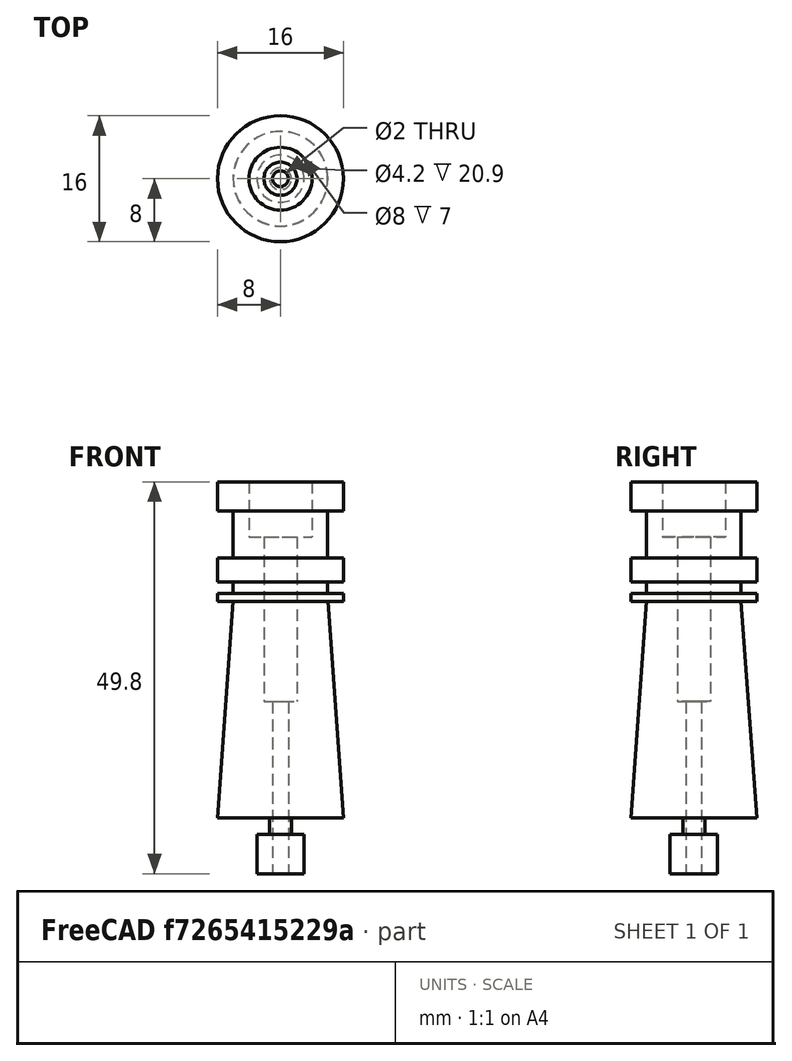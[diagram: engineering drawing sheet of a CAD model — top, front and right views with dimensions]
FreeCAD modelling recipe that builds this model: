
FCSTD DOCUMENT  (FreeCAD 0.15R4671 (Git))
Label: e3d_cuerpo
License: CreativeCommons Attribution-ShareAlike
LicenseURL: http://creativecommons.org/licenses/by-sa/4.0/
objects: Sketcher::SketchObject×1, PartDesign::Revolution×1, Part::Feature×1
note: 4 computed .brp shape members not serialized (recipe doc carries the construction recipe); baked Part::Feature solids carry a one-line shape summary decoded from their .brp

FEATURE [Sketcher::SketchObject] Sketch
  Placement = pos=(0,0,0) rot=(1,0,0;1.5708rad)
  sketch-geometry (24):
    g0: LineSegment StartX=-4 StartY=42.7 StartZ=0 EndX=-8 EndY=42.7 EndZ=0
    g1: LineSegment StartX=-8 StartY=42.7 StartZ=0 EndX=-8 EndY=39 EndZ=0
    g2: LineSegment StartX=-8 StartY=39 StartZ=0 EndX=-6 EndY=39 EndZ=0
    g3: LineSegment StartX=-6 StartY=39 StartZ=0 EndX=-6 EndY=33 EndZ=0
    g4: LineSegment StartX=-6 StartY=33 StartZ=0 EndX=-8 EndY=33 EndZ=0
    g5: LineSegment StartX=-8 StartY=33 StartZ=0 EndX=-8 EndY=30 EndZ=0
    g6: LineSegment StartX=-8 StartY=30 StartZ=0 EndX=-6 EndY=30 EndZ=0
    g7: LineSegment StartX=-6 StartY=30 StartZ=0 EndX=-6 EndY=28.5 EndZ=0
    g8: LineSegment StartX=-6 StartY=28.5 StartZ=0 EndX=-8 EndY=28.5 EndZ=0
    g9: LineSegment StartX=-8 StartY=28.5 StartZ=0 EndX=-8 EndY=27.5 EndZ=0
    g10: LineSegment StartX=-8 StartY=27.5 StartZ=0 EndX=-6.02069 EndY=27.5 EndZ=0
    g11: LineSegment StartX=-6.02069 StartY=27.5 StartZ=0 EndX=-8 EndY=0 EndZ=0
    g12: LineSegment StartX=-8 StartY=0 StartZ=0 EndX=-1.4 EndY=0 EndZ=0
    g13: LineSegment StartX=-4 StartY=42.7 StartZ=0 EndX=-4 EndY=35.7 EndZ=0
    g14: LineSegment StartX=-4 StartY=35.7 StartZ=0 EndX=-2.1 EndY=35.7 EndZ=0
    g15: LineSegment [constr] StartX=-6 StartY=102.239 StartZ=0 EndX=-6 EndY=-7.39754 EndZ=0
    g16: LineSegment [constr] StartX=-8 StartY=67.1328 StartZ=0 EndX=-8 EndY=-9.08317 EndZ=0
    g17: LineSegment StartX=-1.4 StartY=0 StartZ=0 EndX=-1.4 EndY=-2.1 EndZ=0
    g18: LineSegment StartX=-1.4 StartY=-2.1 StartZ=0 EndX=-3 EndY=-2.1 EndZ=0
    g19: LineSegment StartX=-3 StartY=-2.1 StartZ=0 EndX=-3 EndY=-7.1 EndZ=0
    g20: LineSegment StartX=-3 StartY=-7.1 StartZ=0 EndX=-1 EndY=-7.1 EndZ=0
    g21: LineSegment StartX=-2.1 StartY=35.7 StartZ=0 EndX=-2.1 EndY=14.8 EndZ=0
    g22: LineSegment StartX=-2.1 StartY=14.8 StartZ=0 EndX=-1 EndY=14.8 EndZ=0
    g23: LineSegment StartX=-1 StartY=14.8 StartZ=0 EndX=-1 EndY=-7.1 EndZ=0
  constraints (69):
    c: Horizontal(g0)
    c: Coincident(g0,g1)
    c: Vertical(g1)
    c: Coincident(g1,g2)
    c: Horizontal(g2)
    c: Coincident(g2,g3)
    c: Vertical(g3)
    c: Coincident(g3,g4)
    c: Horizontal(g4)
    c: Coincident(g4,g5)
    c: Vertical(g5)
    c: Coincident(g5,g6)
    c: Horizontal(g6)
    c: Coincident(g6,g7)
    c: Vertical(g7)
    c: Coincident(g7,g8)
    c: Horizontal(g8)
    c: Coincident(g8,g9)
    c: Coincident(g9,g10)
    c: Horizontal(g10)
    c: Coincident(g10,g11)
    c: Coincident(g11,g12)
    c: Horizontal(g12)
    c: Coincident(g0,g13)
    c: Vertical(g13)
    c: Coincident(g13,g14)
    c: DistanceX(g-1,g0) = -4
    c: Horizontal(g14)
    c: DistanceX(g-1,g14) = -2.1
    c: DistanceX(g-1,g0) = -8
    c: Vertical(g9)
    c: DistanceY(g1,g0) = 3.7
    c: DistanceY(g1,g4) = -6
    c: DistanceY(g4,g5) = -3
    c: DistanceX(g-1,g11) = -8
    c: PointOnObject(g12,g-1)
    c: Vertical(g15)
    c: DistanceX(g-1,g15) = -6
    c: PointOnObject(g2,g15)
    c: PointOnObject(g6,g15)
    c: DistanceY(g8,g9) = -1
    c: DistanceY(g12,g0) = 42.7
    c: Vertical(g16)
    c: DistanceX(g-1,g16) = -8
    c: PointOnObject(g9,g16)
    c: PointOnObject(g5,g16)
    c: DistanceY(g8,g5) = 1.5
    c: DistanceY(g0,g14) = -7
    c: Coincident(g12,g17)
    c: Vertical(g17)
    c: Coincident(g17,g18)
    c: Horizontal(g18)
    c: Coincident(g18,g19)
    c: Vertical(g19)
    c: Coincident(g19,g20)
    c: Horizontal(g20)
    c: DistanceY(g17,g12) = 2.1
    c: DistanceY(g18,g19) = -5
    c: DistanceX(g-1,g19) = -3
    c: Coincident(g14,g21)
    c: Vertical(g21)
    c: Coincident(g21,g22)
    c: Coincident(g22,g23)
    c: Coincident(g23,g20)
    c: Vertical(g23)
    c: Horizontal(g22)
    c: DistanceX(g-1,g12) = -1.4
    c: DistanceY(g12,g22) = 14.8
    c: DistanceX(g-1,g20) = -1
FEATURE [PartDesign::Revolution] Revolution
  Angle = 360
  Axis = (0,0,1)
  Base = (0,0,0)
  Placement = pos=(0,0,0) rot=(1,0,0;1.5708rad)
  ReferenceAxis = -> Sketch [V_Axis]
  Sketch = -> Sketch
FEATURE [Part::Feature] Revolution001  label="cuerpo"
  Placement = pos=(0,0,0) rot=(1,0,0;1.5708rad)
  shape: bbox 16 x 16 x 49.8 mm, 22 faces (baked)
